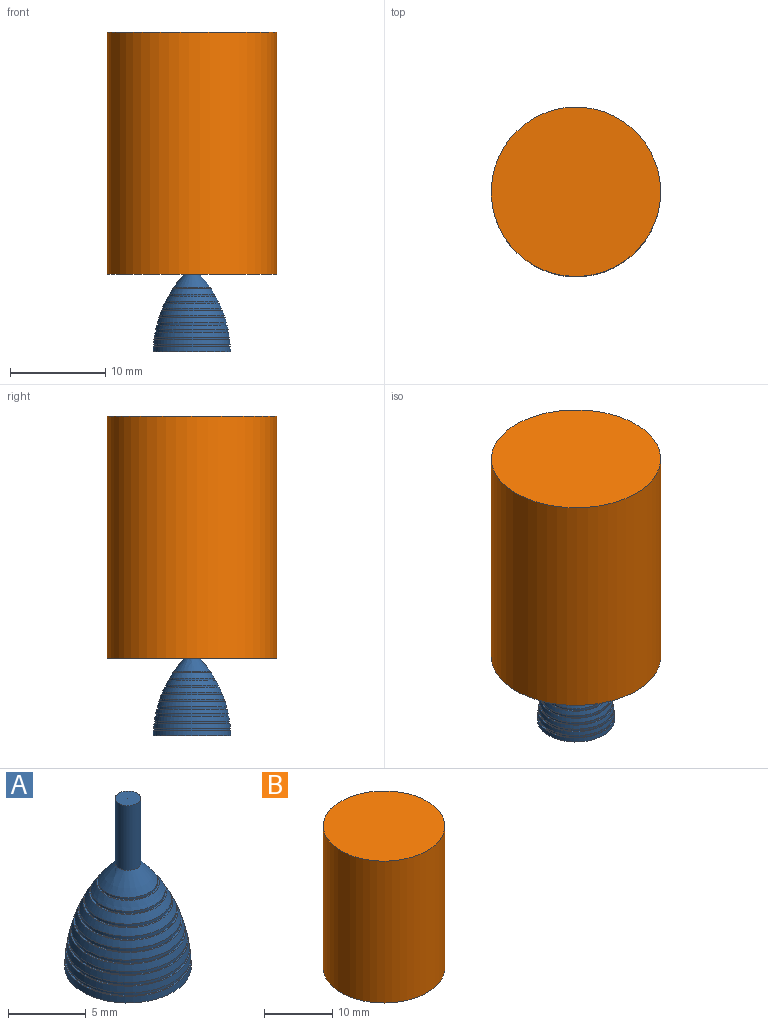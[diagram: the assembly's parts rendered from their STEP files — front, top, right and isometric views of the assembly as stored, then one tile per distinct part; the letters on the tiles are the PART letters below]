
ASSEMBLY  parts=2 mates=1
PART A: 38 faces, bbox 8.1x8.1x13.2 mm
  f0: revolved ~4.76x4.76mm, area 9.6mm2, adj f1,f37
  f1: cylinder r=2.38mm len=4.76mm, axis (0,0,-1), area 2.6mm2, adj f0,f2
  f2: plane 4.96x4.96mm, normal (0,0,1), area 1.6mm2, adj f1,f3
  f3: revolved ~5.56x5.56mm, area 10.4mm2, adj f2,f4
  f4: cylinder r=2.78mm len=5.56mm, axis (0,0,-1), area 3.6mm2, adj f3,f5
  f5: plane 5.76x5.76mm, normal (0,0,1), area 1.8mm2, adj f4,f6
  f6: revolved ~6.22x6.22mm, area 10.6mm2, adj f5,f7
  f7: cylinder r=3.11mm len=6.22mm, axis (0,0,-1), area 4.9mm2, adj f6,f8
  f8: plane 6.42x6.42mm, normal (0,0,1), area 2mm2, adj f7,f9
  f9: revolved ~6.8x6.8mm, area 11.3mm2, adj f8,f10
  f10: plane 6.8x6.8mm, normal (0,0,-1), area 0.4mm2, adj f9,f11
  f11: cylinder r=3.38mm len=6.76mm, axis (0,0,-1), area 5.4mm2, adj f10,f12
  f12: plane 6.97x6.97mm, normal (0,0,1), area 2.2mm2, adj f11,f13
  f13: revolved ~7.27x7.27mm, area 11.9mm2, adj f12,f14
  f14: plane 7.27x7.27mm, normal (0,0,-1), area 0.8mm2, adj f13,f15
  f15: cylinder r=3.6mm len=7.2mm, axis (0,0,-1), area 5.7mm2, adj f14,f16
  f16: plane 7.4x7.4mm, normal (0,0,1), area 2.3mm2, adj f15,f17
  f17: revolved ~7.63x7.63mm, area 12.3mm2, adj f16,f18
  f18: plane 7.63x7.63mm, normal (0,0,-1), area 1.2mm2, adj f17,f19
  f19: cylinder r=3.76mm len=7.53mm, axis (0,0,-1), area 6mm2, adj f18,f20
  f20: plane 7.73x7.73mm, normal (0,0,1), area 2.4mm2, adj f19,f21
  f21: revolved ~7.9x7.9mm, area 12.6mm2, adj f20,f22
  f22: plane 7.9x7.9mm, normal (0,0,-1), area 1.7mm2, adj f21,f23
  f23: cylinder r=3.88mm len=7.76mm, axis (0,0,-1), area 6.2mm2, adj f22,f24
  f24: plane 7.96x7.96mm, normal (0,0,1), area 2.5mm2, adj f23,f25
  f25: revolved ~8.06x8.06mm, area 12.9mm2, adj f24,f26
  f26: plane 8.06x8.06mm, normal (0,0,-1), area 2.1mm2, adj f25,f27
  f27: cylinder r=3.94mm len=7.89mm, axis (0,0,-1), area 6.3mm2, adj f26,f28
  f28: plane 8.09x8.09mm, normal (0,0,1), area 2.6mm2, adj f27,f29
  f29: revolved ~8.13x8.13mm, area 13mm2, adj f28,f30
  f30: plane 8.13x8.13mm, normal (0,0,-1), area 8mm2, adj f29,f31
  f31: revolved ~7.8x7.48mm, area 146.8mm2, adj f30,f32
  f32: plane 1.41x1.41mm, normal (0,0,-1), area 1.6mm2, adj f31
  f33: cone r=0.81mm half-angle=89.8deg, axis (0,0,-1), area 2.1mm2, adj f34
  f34: cylinder r=0.81mm len=5.08mm, axis (0,0,-1), area 25.9mm2, adj f33,f35
  f35: revolved ~3.82x3.82mm, area 15.2mm2, adj f34,f36
  f36: cylinder r=1.91mm len=3.82mm, axis (0,0,-1), area 1.8mm2, adj f35,f37
  f37: plane 4.03x4.03mm, normal (0,0,1), area 1.3mm2, adj f0,f36
PART B: 5 faces, bbox 17.8x17.8x25.4 mm
  f0: cylinder r=8.89mm len=25.4mm, axis (0,0,-1), area 1418.8mm2, adj f1,f2
  f1: plane 17.78x17.78mm, normal (0,0,1), area 248.3mm2, adj f0
  f2: plane 17.78x17.78mm, normal (0,0,-1), area 246.2mm2, adj f0,f3
  f3: cylinder r=0.81mm len=5.08mm, axis (0,0,-1), area 25.9mm2, adj f2,f4
  f4: plane 1.63x1.63mm, normal (0,0,-1), area 2.1mm2, adj f3
PLACE A t=(-2.45,-137.98,-23.27)mm
PLACE B t=(-17.8,55.57,4.66)mm
MATE fastened A.f1 <-> B.f0  axis (0,0,-1) through (-83.05,-36.38,9.74)mm
